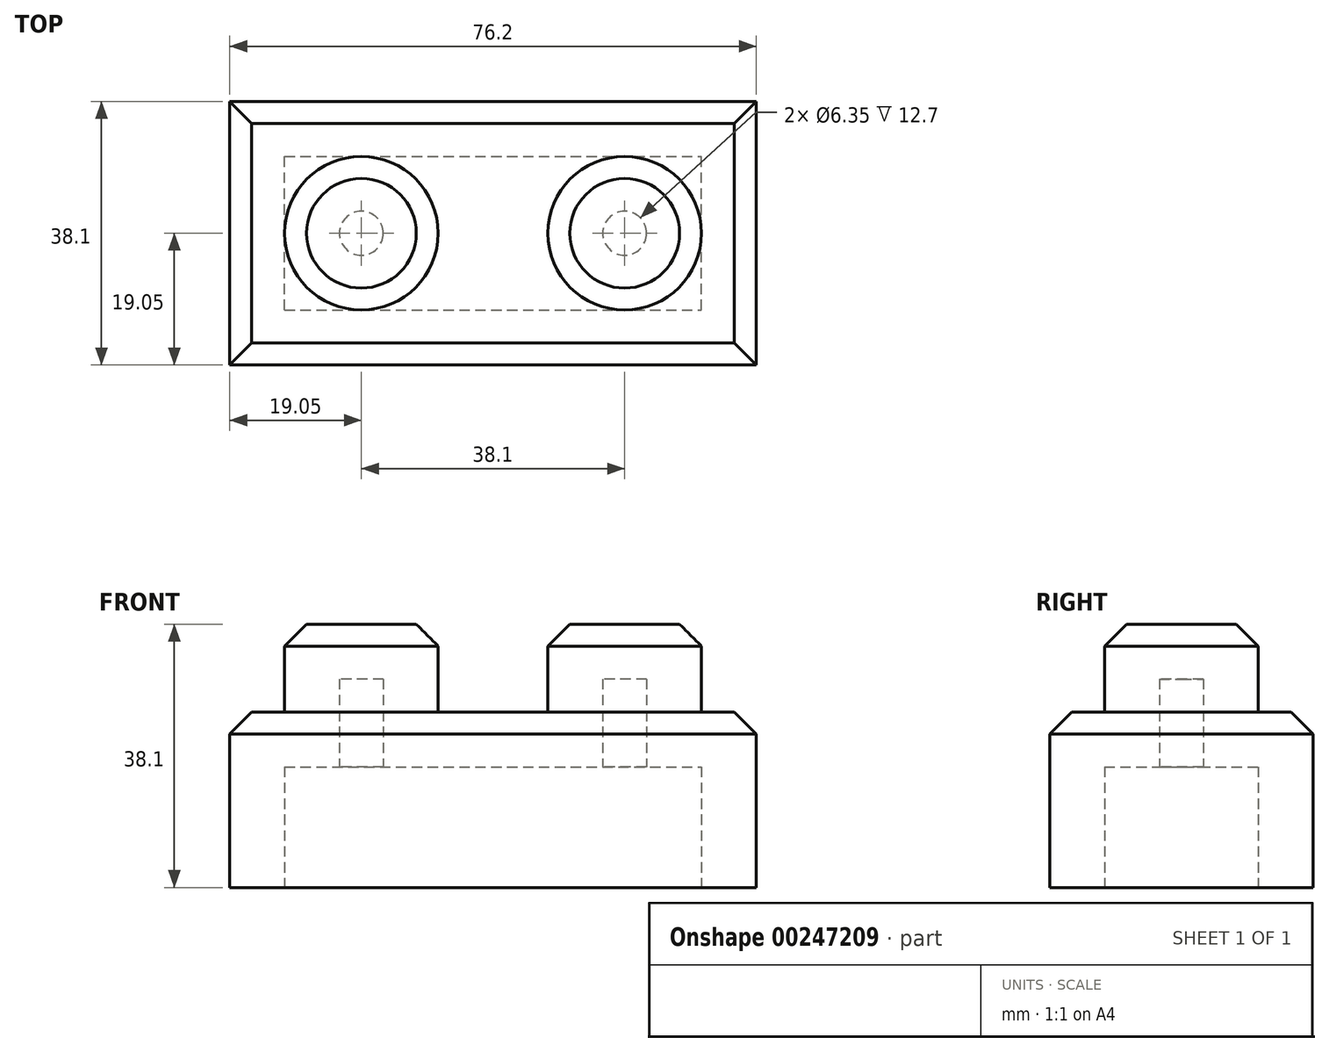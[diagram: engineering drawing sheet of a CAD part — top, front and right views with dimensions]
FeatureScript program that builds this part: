
annotation { "Feature Type Name" : "Feature", "Feature Type Description" : "" }
export const myFeature = defineFeature(function(context is Context, id is Id, definition is map)
    precondition{}
    {
        {
            var Q0;
            Q0=qCreatedBy(makeId("Top.planeOp"),FACE);
            var sketch = newSketch(context, id + "F0", { "sketchPlane" : qUnion([Q0])});
            skLineSegment(sketch, "E0.bottom", {"start": v(0, 0) * mm, "end": v(76.2, 0) * mm});
            skLineSegment(sketch, "E0.top", {"start": v(0, 38.1) * mm, "end": v(76.2, 38.1) * mm});
            skLineSegment(sketch, "E0.left", {"start": v(0, 0) * mm, "end": v(0, 38.1) * mm});
            skLineSegment(sketch, "E0.right", {"start": v(76.2, 0) * mm, "end": v(76.2, 38.1) * mm});
            skSolve(sketch);
        }
        {
            var Q0;
            Q0 = qSketchRegion(id + "F0", true);
            extrude(context, id + "F1", {"entities" : qUnion([Q0]), "depth" : 25.4 * mm});
        }
        {
            var Q0;
            Q0=makeQuery(id+"F1.opExtrude","CAP_FACE",FACE,{"disambiguationData":[OSD([sQuery(id+"F0.wireOp",EDGE,"E0.bottom"),sQuery(id+"F0.wireOp",EDGE,"E0.top"),sQuery(id+"F0.wireOp",EDGE,"E0.left"),sQuery(id+"F0.wireOp",EDGE,"E0.right")])],"isStart":false});
            var sketch = newSketch(context, id + "F2", { "sketchPlane" : qUnion([Q0])});
            skCircle(sketch, "E1", {"center": v(19.05, 19.05) * mm, "radius": 11.11 * mm});
            skCircle(sketch, "E2", {"center": v(57.15, 19.05) * mm, "radius": 11.11 * mm});
            skSolve(sketch);
        }
        {
            var Q0;
            Q0=makeQuery(id+"F2.imprint","IMPRINT",FACE,{"disambiguationData":[TD([[makeQuery(id+"F2.imprint","IMPRINT",EDGE,{"derivedFrom":sQuery(id+"F2.wireOp",EDGE,"E2")}),1.0]])]});
            var Q1;
            Q1=makeQuery(id+"F2.imprint","IMPRINT",FACE,{"disambiguationData":[TD([[makeQuery(id+"F2.imprint","IMPRINT",EDGE,{"derivedFrom":sQuery(id+"F2.wireOp",EDGE,"E1")}),1.0]])]});
            extrude(context, id + "F3", {"entities" : qUnion([Q0, Q1]), "operationType" : NewBodyOperationType.ADD, "depth" : 12.7 * mm});
        }
        {
            var Q0;
            Q0=makeQuery(id+"F1.opExtrude","CAP_FACE",FACE,{"disambiguationData":[OSD([sQuery(id+"F0.wireOp",EDGE,"E0.bottom"),sQuery(id+"F0.wireOp",EDGE,"E0.top"),sQuery(id+"F0.wireOp",EDGE,"E0.left"),sQuery(id+"F0.wireOp",EDGE,"E0.right")])],"isStart":true});
            shell(context, id + "F4", {"entities" : qUnion([Q0]), "thickness" : 7.94 * mm});
        }
        {
            var Q0;
            Q0=makeQuery(id+"F1.opExtrude","CAP_EDGE",EDGE,{"disambiguationData":[OSD([sQuery(id+"F0.wireOp",EDGE,"E0.bottom")])],"isStart":false});
            var Q1;
            Q1=makeQuery(id+"F1.opExtrude","CAP_EDGE",EDGE,{"disambiguationData":[OSD([sQuery(id+"F0.wireOp",EDGE,"E0.left")])],"isStart":false});
            var Q2;
            Q2=makeQuery(id+"F1.opExtrude","CAP_EDGE",EDGE,{"disambiguationData":[OSD([sQuery(id+"F0.wireOp",EDGE,"E0.top")])],"isStart":false});
            var Q3;
            Q3=makeQuery(id+"F3.opExtrude","CAP_EDGE",EDGE,{"disambiguationData":[OSD([sQuery(id+"F2.wireOp",EDGE,"E1")])],"isStart":false});
            var Q4;
            Q4=makeQuery(id+"F3.opExtrude","CAP_EDGE",EDGE,{"disambiguationData":[OSD([sQuery(id+"F2.wireOp",EDGE,"E2")])],"isStart":false});
            var Q5;
            Q5=makeQuery(id+"F1.opExtrude","CAP_EDGE",EDGE,{"disambiguationData":[OSD([sQuery(id+"F0.wireOp",EDGE,"E0.right")])],"isStart":false});
            chamfer(context, id + "F5", {"entities" : qUnion([Q0, Q1, Q2, Q3, Q4, Q5]), "width" : 3.17 * mm, "tangentPropagation" : true});
        }
    });
